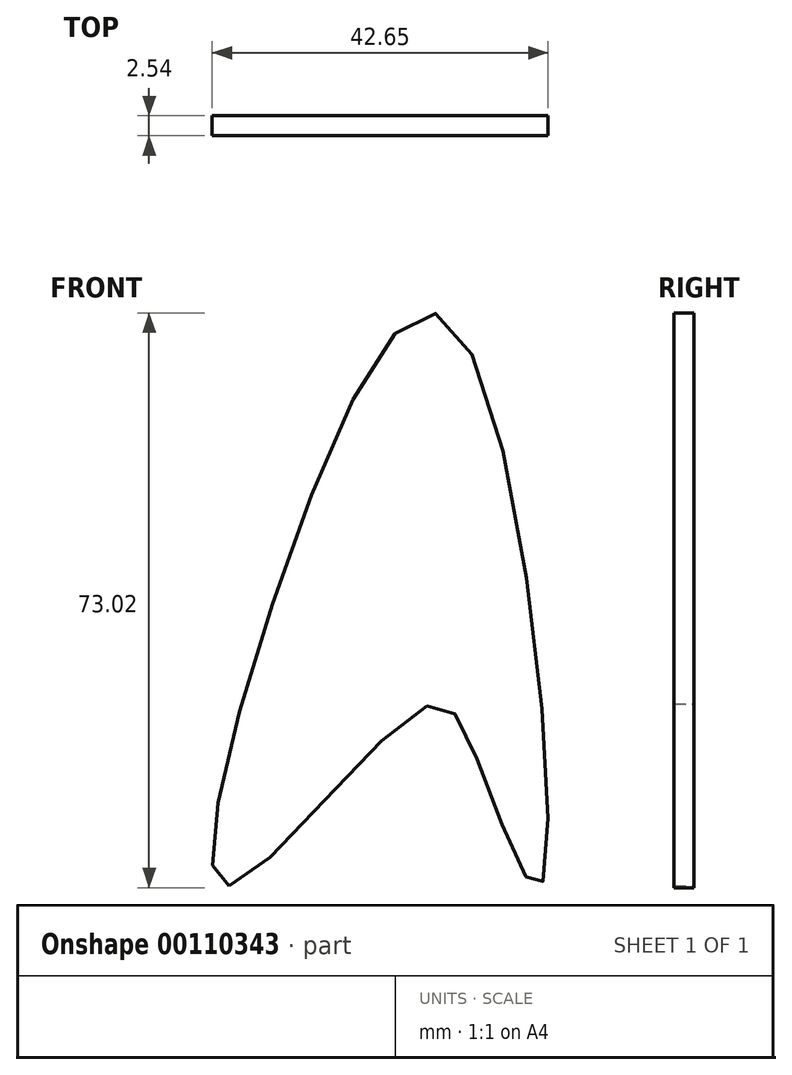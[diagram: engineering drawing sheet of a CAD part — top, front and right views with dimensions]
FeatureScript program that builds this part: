
annotation { "Feature Type Name" : "Feature", "Feature Type Description" : "" }
export const myFeature = defineFeature(function(context is Context, id is Id, definition is map)
    precondition{}
    {
        {
            var Q0;
            Q0=qCreatedBy(makeId("Front.planeOp"),FACE);
            var sketch = newSketch(context, id + "F0", { "sketchPlane" : qUnion([Q0])});
            skFitSpline(sketch, "E0", {"points": [v(0, 0) * mm, v(6.87, 39.85) * mm, v(28.4, 71.36) * mm, v(39.54, 0) * mm, v(31.03, 17.23) * mm, v(24.66, 22.65) * mm, v(0, 0) * mm]});
            skSolve(sketch);
        }
        {
            var Q0;
            Q0=qSketchRegion(id+"F0",true);
            extrude(context, id + "F1", {"entities" : qUnion([Q0]), "depth" : 2.54 * mm});
        }
    });
